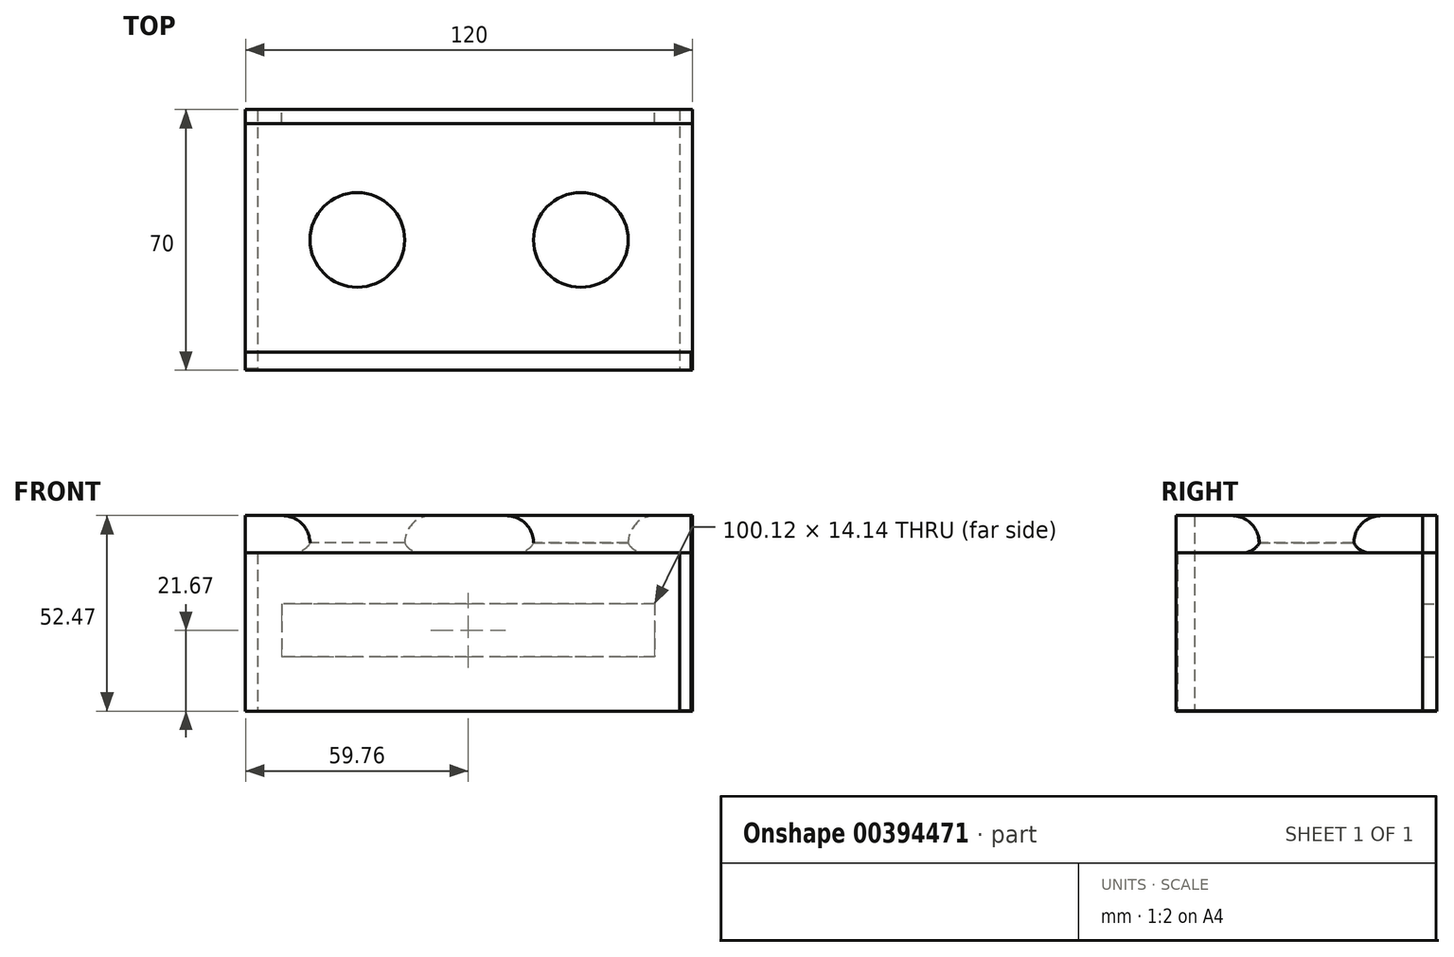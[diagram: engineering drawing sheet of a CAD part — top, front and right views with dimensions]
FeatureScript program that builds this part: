
annotation { "Feature Type Name" : "Feature", "Feature Type Description" : "" }
export const myFeature = defineFeature(function(context is Context, id is Id, definition is map)
    precondition{}
    {
        {
            var Q0;
            Q0=qCreatedBy(makeId("Top.planeOp"),FACE);
            var sketch = newSketch(context, id + "F0", { "sketchPlane" : qUnion([Q0])});
            skLineSegment(sketch, "E0.bottom", {"start": v(-70.16, 19.39) * mm, "end": v(49.84, 19.39) * mm});
            skLineSegment(sketch, "E0.top", {"start": v(-70.16, -50.61) * mm, "end": v(49.84, -50.61) * mm});
            skLineSegment(sketch, "E0.left", {"start": v(-70.16, 19.39) * mm, "end": v(-70.16, -50.61) * mm});
            skLineSegment(sketch, "E0.right", {"start": v(49.84, 19.39) * mm, "end": v(49.84, -50.61) * mm});
            skLineSegment(sketch, "E1", {"start": v(-10.16, -50.61) * mm, "end": v(-10.16, 19.39) * mm});
            skLineSegment(sketch, "E2", {"start": v(-70.16, -15.61) * mm, "end": v(49.84, -15.61) * mm, "construction": true});
            skLineSegment(sketch, "E3", {"start": v(-70.16, -15.61) * mm, "end": v(-10.16, -15.61) * mm, "construction": true});
            skLineSegment(sketch, "E4", {"start": v(-40.16, 19.39) * mm, "end": v(-40.16, -50.61) * mm, "construction": true});
            skPoint(sketch, "E4.startSnap0", {"position": v(-40.16, -15.61) * mm});
            skCircle(sketch, "E5", {"center": v(-40.16, -15.61) * mm, "radius": 12.7 * mm});
            skLineSegment(sketch, "E6", {"start": v(-10.16, 19.39) * mm, "end": v(49.84, 19.39) * mm, "construction": true});
            skLineSegment(sketch, "E7", {"start": v(49.84, -50.61) * mm, "end": v(-10.16, -50.61) * mm, "construction": true});
            skLineSegment(sketch, "E8", {"start": v(19.84, -50.61) * mm, "end": v(19.84, 19.39) * mm, "construction": true});
            skCircle(sketch, "E9", {"center": v(19.84, -15.61) * mm, "radius": 12.7 * mm});
            skSolve(sketch);
        }
        {
            var Q0;
            {var subQ0=sQuery(id+"F0.wireOp",EDGE,"E0.right");Q0=makeQuery(id+"F0.imprint","IMPRINT",FACE,{"disambiguationData":[TD([[makeQuery(id+"F0.imprint","IMPRINT",EDGE,{"derivedFrom":subQ0}),-1.0]])]});}
            var Q1;
            {var subQ1=sQuery(id+"F0.wireOp",EDGE,"E0.left");Q1=makeQuery(id+"F0.imprint","IMPRINT",FACE,{"disambiguationData":[TD([[makeQuery(id+"F0.imprint","IMPRINT",EDGE,{"derivedFrom":subQ1}),1.0]])]});}
            extrude(context, id + "F1", {"entities" : qUnion([Q0, Q1]), "depth" : 10 * mm});
        }
        {
            var Q0;
            Q0=makeQuery(id+"F1.opExtrude","CAP_EDGE",EDGE,{"disambiguationData":[OSD([sQuery(id+"F0.wireOp",EDGE,"E5")])],"isStart":false});
            var Q1;
            Q1=makeQuery(id+"F1.opExtrude","CAP_EDGE",EDGE,{"disambiguationData":[OSD([sQuery(id+"F0.wireOp",EDGE,"E9")])],"isStart":false});
            fillet(context, id + "F2", {"entities" : qUnion([Q0, Q1]), "radius" : 7.36 * mm, "tangentPropagation" : true, "allowEdgeOverflow" : false});
        }
        {
            var Q0;
            Q0=makeQuery(id+"F1.opExtrude","CAP_EDGE",EDGE,{"disambiguationData":[OSD([sQuery(id+"F0.wireOp",EDGE,"E5")])],"isStart":true});
            var Q1;
            Q1=makeQuery(id+"F1.opExtrude","CAP_EDGE",EDGE,{"disambiguationData":[OSD([sQuery(id+"F0.wireOp",EDGE,"E9")])],"isStart":true});
            fillet(context, id + "F3", {"entities" : qUnion([Q0, Q1]), "radius" : 5.08 * mm, "tangentPropagation" : true, "allowEdgeOverflow" : false});
        }
        {
            var Q0;
            Q0=makeQuery(id+"F1.opExtrude","SWEPT_FACE",FACE,{"disambiguationData":[OSD([sQuery(id+"F0.wireOp",EDGE,"E0.left")])]});
            var sketch = newSketch(context, id + "F4", { "sketchPlane" : qUnion([Q0])});
            skLineSegment(sketch, "E10.bottom", {"start": v(50.18, 10.14) * mm, "end": v(-19.22, 10.14) * mm});
            skLineSegment(sketch, "E10.top", {"start": v(50.18, -42.47) * mm, "end": v(-19.22, -42.47) * mm});
            skLineSegment(sketch, "E10.left", {"start": v(50.18, 10.14) * mm, "end": v(50.18, -42.47) * mm});
            skLineSegment(sketch, "E10.right", {"start": v(-19.22, 10.14) * mm, "end": v(-19.22, -42.47) * mm});
            skSolve(sketch);
        }
        {
            var Q0;
            {var subQ0=sQuery(id+"F4.wireOp",EDGE,"E10.top");Q0=makeQuery(id+"F4.imprint","IMPRINT",FACE,{"disambiguationData":[TD([[makeQuery(id+"F4.imprint","IMPRINT",EDGE,{"derivedFrom":subQ0}),-1.0]])]});}
            extrude(context, id + "F5", {"entities" : qUnion([Q0]), "operationType" : NewBodyOperationType.ADD, "oppositeDirection" : true, "depth" : 3.3 * mm});
        }
        {
            var Q0;
            Q0=makeQuery(id+"F1.opExtrude","SWEPT_FACE",FACE,{"disambiguationData":[OSD([sQuery(id+"F0.wireOp",EDGE,"E0.bottom")])]});
            var sketch = newSketch(context, id + "F6", { "sketchPlane" : qUnion([Q0])});
            skPoint(sketch, "E11.oppositeSnap0", {"position": v(70.16, 5) * mm});
            skLineSegment(sketch, "E11.bottom", {"start": v(-49.84, 10) * mm, "end": v(70.16, 10) * mm});
            skLineSegment(sketch, "E11.top", {"start": v(-49.84, -42.47) * mm, "end": v(70.16, -42.47) * mm});
            skLineSegment(sketch, "E11.left", {"start": v(-49.84, 10) * mm, "end": v(-49.84, -42.47) * mm});
            skLineSegment(sketch, "E11.right", {"start": v(70.16, 10) * mm, "end": v(70.16, -42.47) * mm});
            skSolve(sketch);
        }
        {
            var Q0;
            Q0 = qSketchRegion(id + "F6", true);
            extrude(context, id + "F7", {"entities" : qUnion([Q0]), "oppositeDirection" : true, "depth" : 3.8 * mm});
        }
        {
            var Q0;
            Q0=makeQuery(id+"F1.opExtrude","CAP_FACE",FACE,{"disambiguationData":[OSD([sQuery(id+"F0.wireOp",EDGE,"E0.bottom"),sQuery(id+"F0.wireOp",EDGE,"E0.top"),sQuery(id+"F0.wireOp",EDGE,"E0.left"),sQuery(id+"F0.wireOp",EDGE,"E0.right"),sQuery(id+"F0.wireOp",EDGE,"E5"),sQuery(id+"F0.wireOp",EDGE,"E9")])],"isStart":true});
            var sketch = newSketch(context, id + "F8", { "sketchPlane" : qUnion([Q0])});
            skLineSegment(sketch, "E12.bottom", {"start": v(49.84, -19.39) * mm, "end": v(46.31, -19.39) * mm});
            skLineSegment(sketch, "E12.top", {"start": v(49.84, 50.61) * mm, "end": v(46.31, 50.61) * mm});
            skLineSegment(sketch, "E12.left", {"start": v(49.84, -19.39) * mm, "end": v(49.84, 50.61) * mm});
            skLineSegment(sketch, "E12.right", {"start": v(46.31, -19.39) * mm, "end": v(46.31, 50.61) * mm});
            skSolve(sketch);
        }
        {
            var Q0;
            Q0=makeQuery(id+"F8.imprint","IMPRINT",FACE,{"disambiguationData":[TD([[makeQuery(id+"F8.imprint","IMPRINT",EDGE,{"derivedFrom":sQuery(id+"F8.wireOp",EDGE,"E12.bottom")}),1.0]])]});
            extrude(context, id + "F9", {"entities" : qUnion([Q0]), "depth" : 42.42 * mm});
        }
        {
            var Q0;
            Q0=makeQuery(id+"F1.opExtrude","SWEPT_FACE",FACE,{"disambiguationData":[OSD([sQuery(id+"F0.wireOp",EDGE,"E0.top")])]});
            var sketch = newSketch(context, id + "F10", { "sketchPlane" : qUnion([Q0])});
            skCircle(sketch, "E13", {"center": v(-63.79, 5.13) * mm, "radius": 2.24 * mm});
            skCircle(sketch, "E14", {"center": v(43.26, 5.13) * mm, "radius": 2.56 * mm});
            skSolve(sketch);
        }
        {
            var Q0;
            Q0=makeQuery(id+"F10.imprint","IMPRINT",FACE,{"disambiguationData":[TD([[makeQuery(id+"F10.imprint","IMPRINT",EDGE,{"derivedFrom":sQuery(id+"F10.wireOp",EDGE,"E13")}),1.0]])]});
            extrude(context, id + "F11", {"entities" : qUnion([Q0]), "operationType" : NewBodyOperationType.ADD, "oppositeDirection" : true, "depth" : 17.68 * mm});
        }
        {
            var Q0;
            {var subQ0=sQuery(id+"F0.wireOp",EDGE,"E0.left");Q0=makeQuery(id+"F5.boolean.opBoolean","MERGE",FACE,{"derivedFrom":[makeQuery(id+"F1.opExtrude","SWEPT_FACE",FACE,{"disambiguationData":[OSD([subQ0])]}),makeQuery(id+"F5.opExtrude","CAP_FACE",FACE,{"disambiguationData":[OSD([subQ0,sQuery(id+"F4.wireOp",EDGE,"E10.top"),sQuery(id+"F4.wireOp",EDGE,"E10.left"),sQuery(id+"F4.wireOp",EDGE,"E10.right")])],"isStart":true})]});}
            var sketch = newSketch(context, id + "F12", { "sketchPlane" : qUnion([Q0])});
            skLineSegment(sketch, "E15.bottom", {"start": v(50.61, 10) * mm, "end": v(45.7, 10) * mm});
            skLineSegment(sketch, "E15.top", {"start": v(50.61, -42.47) * mm, "end": v(45.7, -42.47) * mm});
            skLineSegment(sketch, "E15.left", {"start": v(50.61, 10) * mm, "end": v(50.61, -42.47) * mm});
            skLineSegment(sketch, "E15.right", {"start": v(45.7, 10) * mm, "end": v(45.7, -42.47) * mm});
            skSolve(sketch);
        }
        {
            var Q0;
            Q0 = qSketchRegion(id + "F12", true);
            extrude(context, id + "F13", {"entities" : qUnion([Q0]), "oppositeDirection" : true, "depth" : 119.63 * mm});
        }
        {
            var Q0;
            Q0=makeQuery(id+"F7.opExtrude","CAP_FACE",FACE,{"disambiguationData":[OSD([sQuery(id+"F6.wireOp",EDGE,"E11.bottom"),sQuery(id+"F6.wireOp",EDGE,"E11.top"),sQuery(id+"F6.wireOp",EDGE,"E11.left"),sQuery(id+"F6.wireOp",EDGE,"E11.right")])],"isStart":true});
            var sketch = newSketch(context, id + "F14", { "sketchPlane" : qUnion([Q0])});
            skLineSegment(sketch, "E16.bottom", {"start": v(-39.66, -13.73) * mm, "end": v(60.46, -13.73) * mm});
            skLineSegment(sketch, "E16.top", {"start": v(-39.66, -27.87) * mm, "end": v(60.46, -27.87) * mm});
            skLineSegment(sketch, "E16.left", {"start": v(-39.66, -13.73) * mm, "end": v(-39.66, -27.87) * mm});
            skLineSegment(sketch, "E16.right", {"start": v(60.46, -13.73) * mm, "end": v(60.46, -27.87) * mm});
            skSolve(sketch);
        }
        {
            var Q0;
            Q0=makeQuery(id+"F14.imprint","IMPRINT",FACE,{"disambiguationData":[TD([[makeQuery(id+"F14.imprint","IMPRINT",EDGE,{"derivedFrom":sQuery(id+"F14.wireOp",EDGE,"E16.bottom")}),-1.0]])]});
            extrude(context, id + "F15", {"entities" : qUnion([Q0]), "operationType" : NewBodyOperationType.REMOVE, "oppositeDirection" : true, "depth" : 16.26 * mm});
        }
    });
